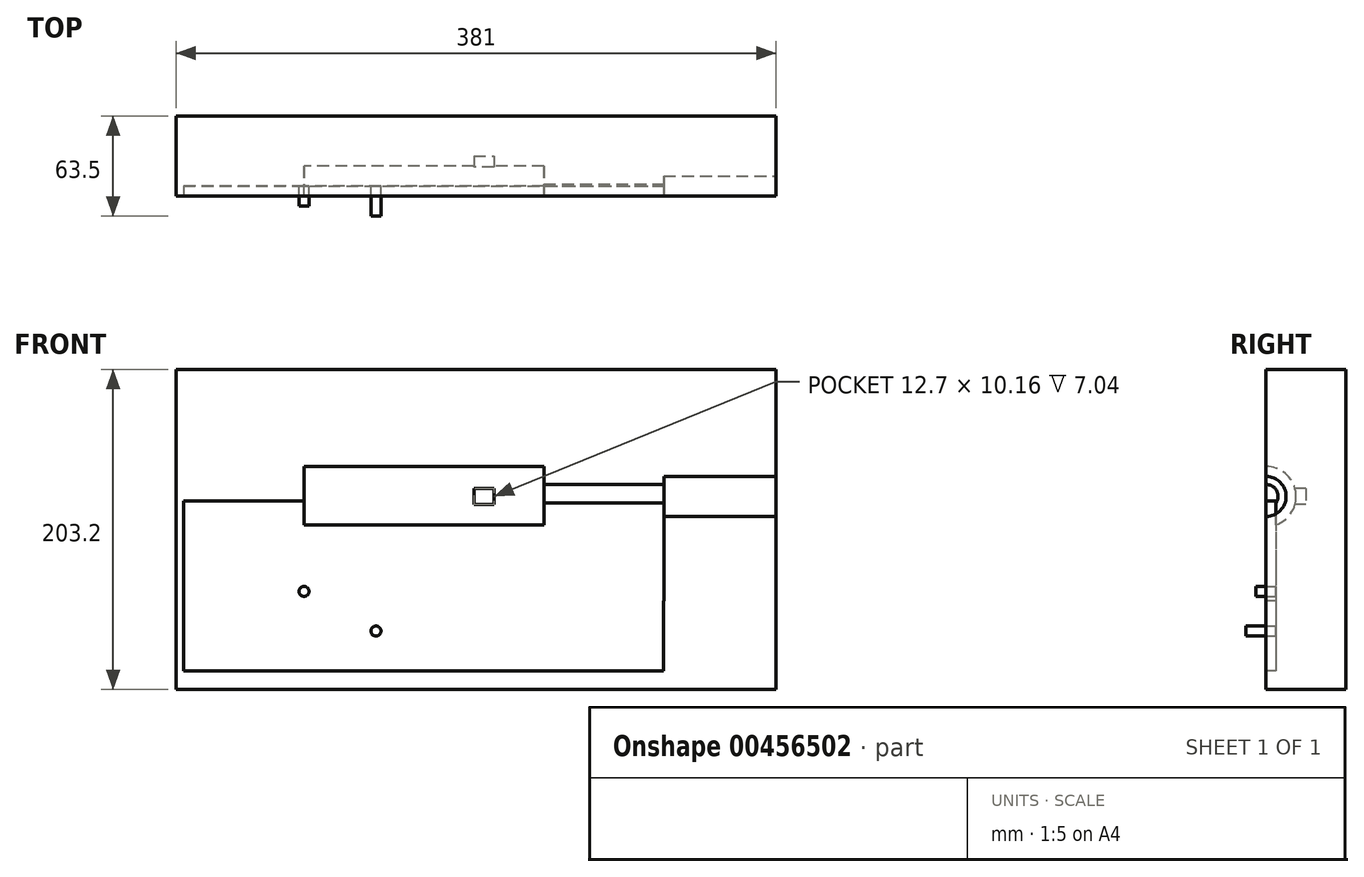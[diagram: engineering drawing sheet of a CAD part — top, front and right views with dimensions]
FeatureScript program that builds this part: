
annotation { "Feature Type Name" : "Feature", "Feature Type Description" : "" }
export const myFeature = defineFeature(function(context is Context, id is Id, definition is map)
    precondition{}
    {
        {
            var Q0;
            Q0=qCreatedBy(makeId("Front.planeOp"),FACE);
            var sketch = newSketch(context, id + "F0", { "sketchPlane" : qUnion([Q0])});
            skLineSegment(sketch, "E0.bottom", {"start": v(147.37, 80.63) * mm, "end": v(-157.43, 80.63) * mm});
            skLineSegment(sketch, "E0.top", {"start": v(147.37, -71.77) * mm, "end": v(-157.43, -71.77) * mm});
            skLineSegment(sketch, "E0.left", {"start": v(147.37, 80.63) * mm, "end": v(147.37, -71.77) * mm});
            skLineSegment(sketch, "E0.right", {"start": v(-157.43, 80.63) * mm, "end": v(-157.43, -71.77) * mm});
            skSolve(sketch);
        }
        {
            var Q0;
            Q0=makeQuery(id+"F0.imprint","IMPRINT",FACE,{"disambiguationData":[TD([[makeQuery(id+"F0.imprint","IMPRINT",EDGE,{"derivedFrom":sQuery(id+"F0.wireOp",EDGE,"E0.bottom")}),1.0]])]});
            extrude(context, id + "F1", {"entities" : qUnion([Q0]), "depth" : 50.8 * mm});
        }
        {
            var Q0;
            Q0=makeQuery(id+"F1.opExtrude","CAP_FACE",FACE,{"disambiguationData":[OSD([sQuery(id+"F0.wireOp",EDGE,"E0.bottom"),sQuery(id+"F0.wireOp",EDGE,"E0.top"),sQuery(id+"F0.wireOp",EDGE,"E0.left"),sQuery(id+"F0.wireOp",EDGE,"E0.right")])],"isStart":false});
            var sketch = newSketch(context, id + "F2", { "sketchPlane" : qUnion([Q0])});
            skLineSegment(sketch, "E1", {"start": v(0, 0) * mm, "end": v(0, -19.05) * mm});
            skLineSegment(sketch, "E2", {"start": v(0, -19.05) * mm, "end": v(-152.4, -19.05) * mm});
            skLineSegment(sketch, "E3", {"start": v(0, 0) * mm, "end": v(-152.4, 0) * mm});
            skLineSegment(sketch, "E4", {"start": v(-152.4, 0) * mm, "end": v(-152.4, -19.05) * mm});
            skSolve(sketch);
        }
        {
            var Q0;
            Q0=makeQuery(id+"F2.imprint","IMPRINT",FACE,{"disambiguationData":[TD([[makeQuery(id+"F2.imprint","IMPRINT",EDGE,{"derivedFrom":sQuery(id+"F2.wireOp",EDGE,"E1")}),-1.0]])]});
            var Q1;
            Q1=sQuery(id+"F2.wireOp",EDGE,"E3");
            revolve(context, id + "F3", {"operationType" : NewBodyOperationType.REMOVE, "entities" : qUnion([Q0]), "axis" : qUnion([Q1]), "revolveType" : RevolveType.FULL, "oppositeDirection" : true});
        }
        {
            var Q0;
            Q0=makeQuery(id+"F1.opExtrude","CAP_FACE",FACE,{"disambiguationData":[OSD([sQuery(id+"F0.wireOp",EDGE,"E0.bottom"),sQuery(id+"F0.wireOp",EDGE,"E0.top"),sQuery(id+"F0.wireOp",EDGE,"E0.left"),sQuery(id+"F0.wireOp",EDGE,"E0.right")])],"isStart":false});
            var sketch = newSketch(context, id + "F4", { "sketchPlane" : qUnion([Q0])});
            skLineSegment(sketch, "E5", {"start": v(0, 0) * mm, "end": v(-31.75, 0) * mm});
            skLineSegment(sketch, "E6", {"start": v(-31.75, 0) * mm, "end": v(-44.45, 0) * mm});
            skLineSegment(sketch, "E7", {"start": v(-31.75, 0) * mm, "end": v(-31.75, 5.08) * mm});
            skLineSegment(sketch, "E8", {"start": v(-31.75, 5.08) * mm, "end": v(-44.45, 5.08) * mm});
            skLineSegment(sketch, "E9", {"start": v(-44.45, 5.08) * mm, "end": v(-44.45, 0) * mm});
            skLineSegment(sketch, "E10", {"start": v(-44.45, 0) * mm, "end": v(-44.45, -5.08) * mm});
            skLineSegment(sketch, "E11", {"start": v(-44.45, -5.08) * mm, "end": v(-31.75, -5.08) * mm});
            skLineSegment(sketch, "E12", {"start": v(-31.75, -5.08) * mm, "end": v(-31.75, 0) * mm});
            skSolve(sketch);
        }
        {
            var Q0;
            Q0=makeQuery(id+"F4.imprint","IMPRINT",FACE,{"disambiguationData":[TD([[makeQuery(id+"F4.imprint","IMPRINT",EDGE,{"derivedFrom":sQuery(id+"F4.wireOp",EDGE,"E6")}),-1.0]])]});
            var Q1;
            Q1=makeQuery(id+"F4.imprint","IMPRINT",FACE,{"disambiguationData":[TD([[makeQuery(id+"F4.imprint","IMPRINT",EDGE,{"derivedFrom":sQuery(id+"F4.wireOp",EDGE,"E6")}),1.0]])]});
            extrude(context, id + "F5", {"entities" : qUnion([Q0, Q1]), "operationType" : NewBodyOperationType.REMOVE, "oppositeDirection" : true, "depth" : 25.4 * mm});
        }
        {
            var Q0;
            Q0=makeQuery(id+"F1.opExtrude","CAP_FACE",FACE,{"disambiguationData":[OSD([sQuery(id+"F0.wireOp",EDGE,"E0.bottom"),sQuery(id+"F0.wireOp",EDGE,"E0.top"),sQuery(id+"F0.wireOp",EDGE,"E0.left"),sQuery(id+"F0.wireOp",EDGE,"E0.right")])],"isStart":false});
            var sketch = newSketch(context, id + "F6", { "sketchPlane" : qUnion([Q0])});
            skLineSegment(sketch, "E13", {"start": v(0, 0) * mm, "end": v(76.2, 0) * mm});
            skPoint(sketch, "E13.endSnap0", {"position": v(0, 0) * mm});
            skLineSegment(sketch, "E14", {"start": v(76.2, -7.62) * mm, "end": v(76.2, 0) * mm});
            skLineSegment(sketch, "E15", {"start": v(76.2, -7.62) * mm, "end": v(0, -7.62) * mm});
            skLineSegment(sketch, "E16", {"start": v(0, -7.62) * mm, "end": v(0, 0) * mm});
            skSolve(sketch);
        }
        {
            var Q0;
            Q0 = qSketchRegion(id + "F6", true);
            var Q1;
            Q1=sQuery(id+"F6.wireOp",EDGE,"E13");
            revolve(context, id + "F7", {"operationType" : NewBodyOperationType.REMOVE, "entities" : qUnion([Q0]), "axis" : qUnion([Q1]), "revolveType" : RevolveType.FULL, "oppositeDirection" : true});
        }
        {
            var Q0;
            Q0=makeQuery(id+"F1.opExtrude","SWEPT_FACE",FACE,{"disambiguationData":[OSD([sQuery(id+"F0.wireOp",EDGE,"E0.right")])]});
            var sketch = newSketch(context, id + "F8", { "sketchPlane" : qUnion([Q0])});
            skLineSegment(sketch, "E17.bottom", {"start": v(50.8, 80.63) * mm, "end": v(44.45, 80.63) * mm});
            skLineSegment(sketch, "E17.top", {"start": v(50.8, -71.77) * mm, "end": v(44.45, -71.77) * mm});
            skLineSegment(sketch, "E17.left", {"start": v(50.8, 80.63) * mm, "end": v(50.8, -71.77) * mm});
            skLineSegment(sketch, "E17.right", {"start": v(44.45, 80.63) * mm, "end": v(44.45, -71.77) * mm});
            skLineSegment(sketch, "E18.bottom", {"start": v(44.45, 80.63) * mm, "end": v(0, 80.63) * mm});
            skLineSegment(sketch, "E18.top", {"start": v(44.45, -71.77) * mm, "end": v(0, -71.77) * mm});
            skLineSegment(sketch, "E18.right", {"start": v(0, 80.63) * mm, "end": v(0, -71.77) * mm});
            skSolve(sketch);
        }
        {
            var Q0;
            Q0=makeQuery(id+"F1.opExtrude","CAP_FACE",FACE,{"disambiguationData":[OSD([sQuery(id+"F0.wireOp",EDGE,"E0.bottom"),sQuery(id+"F0.wireOp",EDGE,"E0.top"),sQuery(id+"F0.wireOp",EDGE,"E0.left"),sQuery(id+"F0.wireOp",EDGE,"E0.right")])],"isStart":false});
            var sketch = newSketch(context, id + "F9", { "sketchPlane" : qUnion([Q0])});
            skLineSegment(sketch, "E19.bottom", {"start": v(76.2, -2.95) * mm, "end": v(-152.4, -2.95) * mm});
            skLineSegment(sketch, "E19.top", {"start": v(76.2, -66.45) * mm, "end": v(-152.4, -66.45) * mm});
            skLineSegment(sketch, "E19.left", {"start": v(76.2, -2.95) * mm, "end": v(76.2, -66.45) * mm});
            skLineSegment(sketch, "E19.right", {"start": v(-152.4, -2.95) * mm, "end": v(-152.4, -66.45) * mm});
            skLineSegment(sketch, "E20.bottom", {"start": v(-152.4, -2.95) * mm, "end": v(-166.76, -2.95) * mm});
            skLineSegment(sketch, "E20.top", {"start": v(-152.4, -66.45) * mm, "end": v(-166.76, -66.45) * mm});
            skLineSegment(sketch, "E20.right", {"start": v(-166.76, -2.95) * mm, "end": v(-166.76, -66.45) * mm});
            skSolve(sketch);
        }
        {
            var Q0;
            Q0 = qSketchRegion(id + "F9", true);
            extrude(context, id + "F10", {"entities" : qUnion([Q0]), "operationType" : NewBodyOperationType.REMOVE, "oppositeDirection" : true, "depth" : 6.35 * mm});
        }
        {
            var Q0;
            Q0 = qSketchRegion(id + "F8", true);
            extrude(context, id + "F11", {"entities" : qUnion([Q0]), "operationType" : NewBodyOperationType.ADD, "depth" : 76.2 * mm});
        }
        {
            var Q0;
            Q0=makeQuery(id+"F11.boolean.opBoolean","MERGE",FACE,{"derivedFrom":[makeQuery(id+"F1.opExtrude","CAP_FACE",FACE,{"disambiguationData":[OSD([sQuery(id+"F0.wireOp",EDGE,"E0.bottom"),sQuery(id+"F0.wireOp",EDGE,"E0.top"),sQuery(id+"F0.wireOp",EDGE,"E0.left"),sQuery(id+"F0.wireOp",EDGE,"E0.right")])],"isStart":false}),makeQuery(id+"F11.opExtrude","SWEPT_FACE",FACE,{"disambiguationData":[OSD([sQuery(id+"F8.wireOp",EDGE,"E17.left")])]})]});
            var sketch = newSketch(context, id + "F12", { "sketchPlane" : qUnion([Q0])});
            skLineSegment(sketch, "E21.bottom", {"start": v(-157.43, -2.95) * mm, "end": v(-228.96, -2.95) * mm});
            skLineSegment(sketch, "E21.top", {"start": v(-157.43, -66.45) * mm, "end": v(-228.96, -66.45) * mm});
            skLineSegment(sketch, "E21.left", {"start": v(-157.43, -2.95) * mm, "end": v(-157.43, -66.45) * mm});
            skLineSegment(sketch, "E21.right", {"start": v(-228.96, -2.95) * mm, "end": v(-228.96, -66.45) * mm});
            skSolve(sketch);
        }
        {
            var Q0;
            Q0=makeQuery(id+"F12.imprint","IMPRINT",FACE,{"disambiguationData":[TD([[makeQuery(id+"F12.imprint","IMPRINT",EDGE,{"derivedFrom":sQuery(id+"F12.wireOp",EDGE,"E21.bottom")}),1.0]])]});
            extrude(context, id + "F13", {"entities" : qUnion([Q0]), "operationType" : NewBodyOperationType.REMOVE, "oppositeDirection" : true, "depth" : 6.35 * mm});
        }
        {
            var Q0;
            Q0=makeQuery(id+"F13.boolean.opBoolean","MERGE",FACE,{"derivedFrom":[makeQuery(id+"F10.boolean.opBoolean","COPY",FACE,{"derivedFrom":makeQuery(id+"F10.opExtrude","CAP_FACE",FACE,{"disambiguationData":[OSD([sQuery(id+"F9.wireOp",EDGE,"E19.bottom"),sQuery(id+"F9.wireOp",EDGE,"E19.top"),sQuery(id+"F9.wireOp",EDGE,"E19.left"),sQuery(id+"F9.wireOp",EDGE,"E20.bottom"),sQuery(id+"F9.wireOp",EDGE,"E20.top"),sQuery(id+"F9.wireOp",EDGE,"E20.right")])],"isStart":false})}),makeQuery(id+"F13.opExtrude","CAP_FACE",FACE,{"disambiguationData":[OSD([sQuery(id+"F12.wireOp",EDGE,"E21.bottom"),sQuery(id+"F12.wireOp",EDGE,"E21.top"),sQuery(id+"F12.wireOp",EDGE,"E21.left"),sQuery(id+"F12.wireOp",EDGE,"E21.right")])],"isStart":false})]});
            var sketch = newSketch(context, id + "F14", { "sketchPlane" : qUnion([Q0])});
            skPoint(sketch, "E22", {"position": v(-152.4, -60.31) * mm});
            skCircle(sketch, "E23", {"center": v(-152.4, -60.31) * mm, "radius": 3.18 * mm});
            skSolve(sketch);
        }
        {
            var Q0;
            Q0=makeQuery(id+"F14.imprint","IMPRINT",FACE,{"disambiguationData":[TD([[makeQuery(id+"F14.imprint","IMPRINT",EDGE,{"derivedFrom":sQuery(id+"F14.wireOp",EDGE,"E23")}),1.0]])]});
            extrude(context, id + "F15", {"entities" : qUnion([Q0]), "operationType" : NewBodyOperationType.ADD, "depth" : 12.7 * mm});
        }
        {
            var Q0;
            Q0=makeQuery(id+"F11.boolean.opBoolean","MERGE",FACE,{"derivedFrom":[makeQuery(id+"F1.opExtrude","SWEPT_FACE",FACE,{"disambiguationData":[OSD([sQuery(id+"F0.wireOp",EDGE,"E0.top")])]}),makeQuery(id+"F11.opExtrude","SWEPT_FACE",FACE,{"disambiguationData":[OSD([sQuery(id+"F8.wireOp",EDGE,"E17.top"),sQuery(id+"F8.wireOp",EDGE,"E18.top")])]})]});
            var sketch = newSketch(context, id + "F16", { "sketchPlane" : qUnion([Q0])});
            skLineSegment(sketch, "E24.bottom", {"start": v(-233.63, 50.8) * mm, "end": v(147.37, 50.8) * mm});
            skLineSegment(sketch, "E24.top", {"start": v(-233.63, 0) * mm, "end": v(147.37, 0) * mm});
            skLineSegment(sketch, "E24.left", {"start": v(-233.63, 50.8) * mm, "end": v(-233.63, 0) * mm});
            skLineSegment(sketch, "E24.right", {"start": v(147.37, 50.8) * mm, "end": v(147.37, 0) * mm});
            skSolve(sketch);
        }
        {
            var Q0;
            Q0=makeQuery(id+"F16.imprint","IMPRINT",FACE,{"disambiguationData":[TD([[makeQuery(id+"F16.imprint","IMPRINT",EDGE,{"derivedFrom":sQuery(id+"F16.wireOp",EDGE,"E24.bottom")}),1.0]])]});
            extrude(context, id + "F17", {"entities" : qUnion([Q0]), "operationType" : NewBodyOperationType.ADD, "depth" : 50.8 * mm});
        }
        {
            var Q0;
            Q0=makeQuery(id+"F17.boolean.opBoolean","MERGE",FACE,{"derivedFrom":[makeQuery(id+"F11.boolean.opBoolean","MERGE",FACE,{"derivedFrom":[makeQuery(id+"F1.opExtrude","CAP_FACE",FACE,{"disambiguationData":[OSD([sQuery(id+"F0.wireOp",EDGE,"E0.bottom"),sQuery(id+"F0.wireOp",EDGE,"E0.top"),sQuery(id+"F0.wireOp",EDGE,"E0.left"),sQuery(id+"F0.wireOp",EDGE,"E0.right")])],"isStart":false}),makeQuery(id+"F11.opExtrude","SWEPT_FACE",FACE,{"disambiguationData":[OSD([sQuery(id+"F8.wireOp",EDGE,"E17.left")])]})]}),makeQuery(id+"F17.opExtrude","SWEPT_FACE",FACE,{"disambiguationData":[OSD([sQuery(id+"F16.wireOp",EDGE,"E24.bottom")])]})]});
            var sketch = newSketch(context, id + "F18", { "sketchPlane" : qUnion([Q0])});
            skLineSegment(sketch, "E25.bottom", {"start": v(-228.96, -66.45) * mm, "end": v(75.84, -66.45) * mm});
            skLineSegment(sketch, "E25.top", {"start": v(-228.96, -110.9) * mm, "end": v(75.84, -110.9) * mm});
            skLineSegment(sketch, "E25.left", {"start": v(-228.96, -66.45) * mm, "end": v(-228.96, -110.9) * mm});
            skLineSegment(sketch, "E25.right", {"start": v(75.84, -66.45) * mm, "end": v(75.84, -110.9) * mm});
            skSolve(sketch);
        }
        {
            var Q0;
            Q0=makeQuery(id+"F18.imprint","IMPRINT",FACE,{"disambiguationData":[TD([[makeQuery(id+"F18.imprint","IMPRINT",EDGE,{"derivedFrom":sQuery(id+"F18.wireOp",EDGE,"E25.bottom")}),1.0]])]});
            extrude(context, id + "F19", {"entities" : qUnion([Q0]), "operationType" : NewBodyOperationType.REMOVE, "oppositeDirection" : true, "depth" : 6.35 * mm});
        }
        {
            var Q0;
            Q0=makeQuery(id+"F19.boolean.opBoolean","MERGE",FACE,{"derivedFrom":[makeQuery(id+"F13.boolean.opBoolean","MERGE",FACE,{"derivedFrom":[makeQuery(id+"F10.boolean.opBoolean","COPY",FACE,{"derivedFrom":makeQuery(id+"F10.opExtrude","CAP_FACE",FACE,{"disambiguationData":[OSD([sQuery(id+"F9.wireOp",EDGE,"E19.bottom"),sQuery(id+"F9.wireOp",EDGE,"E19.top"),sQuery(id+"F9.wireOp",EDGE,"E19.left"),sQuery(id+"F9.wireOp",EDGE,"E20.bottom"),sQuery(id+"F9.wireOp",EDGE,"E20.top"),sQuery(id+"F9.wireOp",EDGE,"E20.right")])],"isStart":false})}),makeQuery(id+"F13.opExtrude","CAP_FACE",FACE,{"disambiguationData":[OSD([sQuery(id+"F12.wireOp",EDGE,"E21.bottom"),sQuery(id+"F12.wireOp",EDGE,"E21.top"),sQuery(id+"F12.wireOp",EDGE,"E21.left"),sQuery(id+"F12.wireOp",EDGE,"E21.right")])],"isStart":false})]}),makeQuery(id+"F19.opExtrude","CAP_FACE",FACE,{"disambiguationData":[OSD([sQuery(id+"F18.wireOp",EDGE,"E25.bottom"),sQuery(id+"F18.wireOp",EDGE,"E25.top"),sQuery(id+"F18.wireOp",EDGE,"E25.left"),sQuery(id+"F18.wireOp",EDGE,"E25.right")])],"isStart":false})]});
            var sketch = newSketch(context, id + "F20", { "sketchPlane" : qUnion([Q0])});
            skPoint(sketch, "E26", {"position": v(-106.71, -85.5) * mm});
            skCircle(sketch, "E27", {"center": v(-106.71, -85.5) * mm, "radius": 3.18 * mm});
            skSolve(sketch);
        }
        {
            var Q0;
            Q0=makeQuery(id+"F20.imprint","IMPRINT",FACE,{"disambiguationData":[TD([[makeQuery(id+"F20.imprint","IMPRINT",EDGE,{"derivedFrom":sQuery(id+"F20.wireOp",EDGE,"E27")}),1.0]])]});
            extrude(context, id + "F21", {"entities" : qUnion([Q0]), "operationType" : NewBodyOperationType.ADD, "depth" : 19.05 * mm});
        }
        {
            var Q0;
            Q0=makeQuery(id+"F17.boolean.opBoolean","MERGE",FACE,{"derivedFrom":[makeQuery(id+"F11.boolean.opBoolean","MERGE",FACE,{"derivedFrom":[makeQuery(id+"F1.opExtrude","CAP_FACE",FACE,{"disambiguationData":[OSD([sQuery(id+"F0.wireOp",EDGE,"E0.bottom"),sQuery(id+"F0.wireOp",EDGE,"E0.top"),sQuery(id+"F0.wireOp",EDGE,"E0.left"),sQuery(id+"F0.wireOp",EDGE,"E0.right")])],"isStart":false}),makeQuery(id+"F11.opExtrude","SWEPT_FACE",FACE,{"disambiguationData":[OSD([sQuery(id+"F8.wireOp",EDGE,"E17.left")])]})]}),makeQuery(id+"F17.opExtrude","SWEPT_FACE",FACE,{"disambiguationData":[OSD([sQuery(id+"F16.wireOp",EDGE,"E24.bottom")])]})]});
            var sketch = newSketch(context, id + "F22", { "sketchPlane" : qUnion([Q0])});
            skLineSegment(sketch, "E28.bottom", {"start": v(76.2, 0) * mm, "end": v(147.37, 0) * mm});
            skLineSegment(sketch, "E28.top", {"start": v(76.2, -12.7) * mm, "end": v(147.37, -12.7) * mm});
            skLineSegment(sketch, "E28.left", {"start": v(76.2, 0) * mm, "end": v(76.2, -12.7) * mm});
            skLineSegment(sketch, "E28.right", {"start": v(147.37, 0) * mm, "end": v(147.37, -12.7) * mm});
            skSolve(sketch);
        }
        {
            var Q0;
            Q0=makeQuery(id+"F22.imprint","IMPRINT",FACE,{"disambiguationData":[TD([[makeQuery(id+"F22.imprint","IMPRINT",EDGE,{"derivedFrom":sQuery(id+"F22.wireOp",EDGE,"E28.bottom")}),-1.0]])]});
            var Q1;
            Q1=sQuery(id+"F22.wireOp",EDGE,"E28.bottom");
            revolve(context, id + "F23", {"operationType" : NewBodyOperationType.REMOVE, "entities" : qUnion([Q0]), "axis" : qUnion([Q1]), "revolveType" : RevolveType.FULL, "oppositeDirection" : true});
        }
        {
            var Q0;
            Q0=makeQuery(id+"F14.imprint","IMPRINT",FACE,{"disambiguationData":[TD([[makeQuery(id+"F14.imprint","IMPRINT",EDGE,{"derivedFrom":sQuery(id+"F14.wireOp",EDGE,"E23")}),1.0]])]});
            extrude(context, id + "F24", {"entities" : qUnion([Q0]), "operationType" : NewBodyOperationType.ADD, "depth" : 6.35 * mm});
        }
    });
